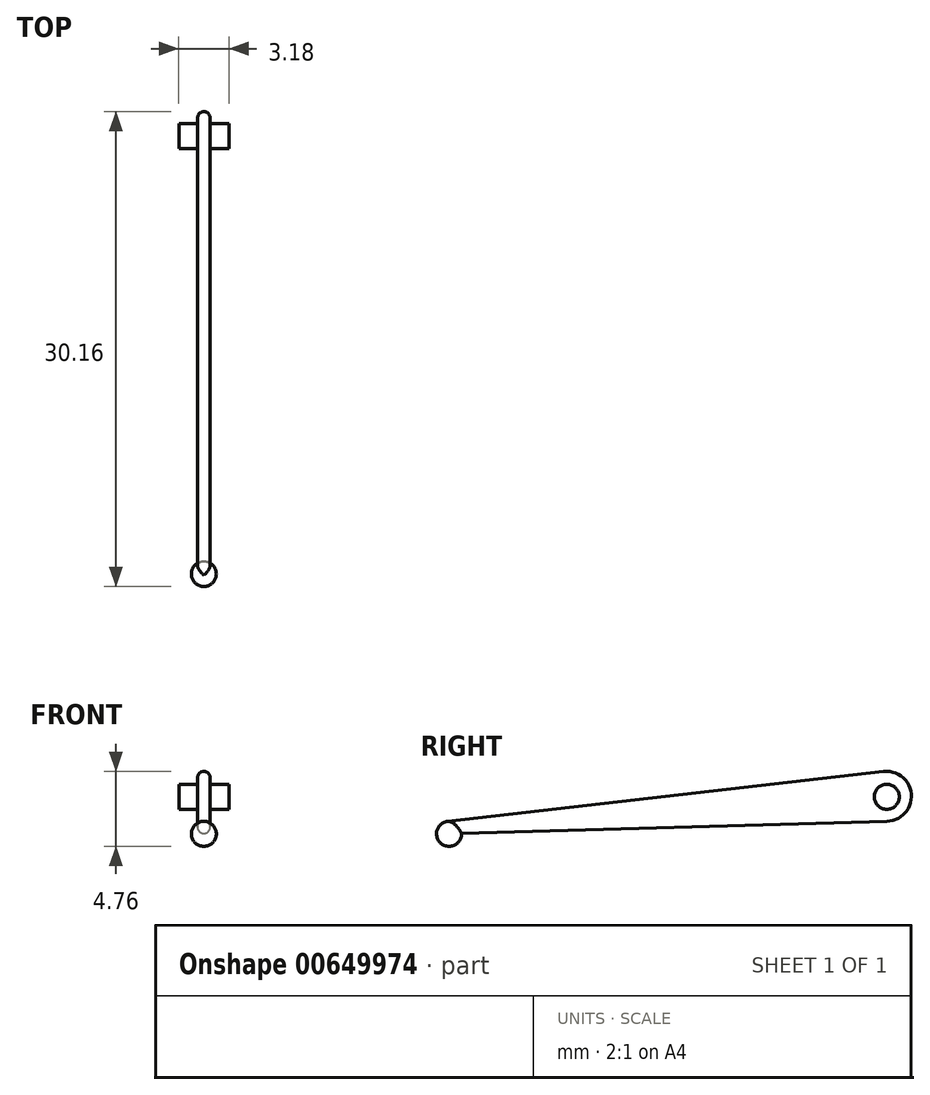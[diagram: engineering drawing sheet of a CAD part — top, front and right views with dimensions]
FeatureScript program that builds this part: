
annotation { "Feature Type Name" : "Feature", "Feature Type Description" : "" }
export const myFeature = defineFeature(function(context is Context, id is Id, definition is map)
    precondition{}
    {
        {
            var Q0;
            Q0=qCreatedBy(makeId("Right.planeOp"),FACE);
            var sketch = newSketch(context, id + "F0", { "sketchPlane" : qUnion([Q0])});
            skCircle(sketch, "E0", {"center": v(3.18, 3.18) * mm, "radius": 1.59 * mm});
            skLineSegment(sketch, "E1", {"start": v(3, 4.75) * mm, "end": v(-24.7, 1.58) * mm});
            skLineSegment(sketch, "E2", {"start": v(-24.6, 0.8) * mm, "end": v(3.22, 1.59) * mm});
            skLineSegment(sketch, "E3", {"start": v(-24.7, 1.58) * mm, "end": v(-24.6, 0.8) * mm});
            skSolve(sketch);
        }
        {
            var Q0;
            Q0=qCreatedBy(makeId("Right.planeOp"),FACE);
            var sketch = newSketch(context, id + "F1", { "sketchPlane" : qUnion([Q0])});
            skCircle(sketch, "E4", {"center": v(3.2, 3.15) * mm, "radius": 0.8 * mm});
            skSolve(sketch);
        }
        {
            var Q0;
            Q0=qCreatedBy(makeId("Right.planeOp"),FACE);
            var sketch = newSketch(context, id + "F2", { "sketchPlane" : qUnion([Q0])});
            skCircle(sketch, "E5", {"center": v(-24.6, 0.8) * mm, "radius": 0.8 * mm});
            skSolve(sketch);
        }
        {
            var Q0;
            Q0 = qSketchRegion(id + "F0", true);
            extrude(context, id + "F3", {"entities" : qUnion([Q0]), "endBound" : BoundingType.SYMMETRIC, "depth" : 0.8 * mm, "offsetDistance" : 25.4 * mm});
        }
        {
            var Q0;
            Q0 = qSketchRegion(id + "F1", true);
            extrude(context, id + "F4", {"entities" : qUnion([Q0]), "operationType" : NewBodyOperationType.ADD, "endBound" : BoundingType.SYMMETRIC, "depth" : 3.17 * mm, "offsetDistance" : 25.4 * mm});
        }
        {
            var Q0;
            Q0=qCreatedBy(makeId("Right.planeOp"),FACE);
            var sketch = newSketch(context, id + "F5", { "sketchPlane" : qUnion([Q0])});
            skArc(sketch, "E6", {"start": v(-25.4, 0.8) * mm, "mid": v(-24.6, 0) * mm, "end": v(-23.81, 0.8) * mm});
            skLineSegment(sketch, "E7", {"start": v(-25.4, 0.8) * mm, "end": v(-23.81, 0.8) * mm});
            skSolve(sketch);
        }
        {
            var Q0;
            Q0=makeQuery(id+"F5.imprint","IMPRINT",FACE,{"disambiguationData":[TD([[makeQuery(id+"F5.imprint","IMPRINT",EDGE,{"derivedFrom":sQuery(id+"F5.wireOp",EDGE,"E6")}),1.0]])]});
            var Q1;
            Q1=sQuery(id+"F5.wireOp",EDGE,"E7");
            revolve(context, id + "F6", {"operationType" : NewBodyOperationType.ADD, "entities" : qUnion([Q0]), "axis" : qUnion([Q1]), "revolveType" : RevolveType.FULL});
        }
        {
            var Q0;
            Q0=makeQuery(id+"F3.opExtrude","CAP_EDGE",EDGE,{"disambiguationData":[OSD([sQuery(id+"F0.wireOp",EDGE,"E1")])],"isStart":true});
            var Q1;
            Q1=makeQuery(id+"F3.opExtrude","CAP_EDGE",EDGE,{"disambiguationData":[OSD([sQuery(id+"F0.wireOp",EDGE,"E0")])],"isStart":true});
            var Q2;
            Q2=makeQuery(id+"F3.opExtrude","CAP_EDGE",EDGE,{"disambiguationData":[OSD([sQuery(id+"F0.wireOp",EDGE,"E2")])],"isStart":true});
            fillet(context, id + "F7", {"entities" : qUnion([Q0, Q1, Q2]), "radius" : 0.4 * mm, "tangentPropagation" : true, "allowEdgeOverflow" : false});
        }
        {
            var Q0;
            Q0=makeQuery(id+"F3.opExtrude","CAP_EDGE",EDGE,{"disambiguationData":[OSD([sQuery(id+"F0.wireOp",EDGE,"E1")])],"isStart":false});
            var Q1;
            Q1=makeQuery(id+"F3.opExtrude","CAP_EDGE",EDGE,{"disambiguationData":[OSD([sQuery(id+"F0.wireOp",EDGE,"E0")])],"isStart":false});
            var Q2;
            Q2=makeQuery(id+"F3.opExtrude","CAP_EDGE",EDGE,{"disambiguationData":[OSD([sQuery(id+"F0.wireOp",EDGE,"E2")])],"isStart":false});
            fillet(context, id + "F8", {"entities" : qUnion([Q0, Q1, Q2]), "radius" : 0.4 * mm, "tangentPropagation" : true, "allowEdgeOverflow" : false});
        }
    });
